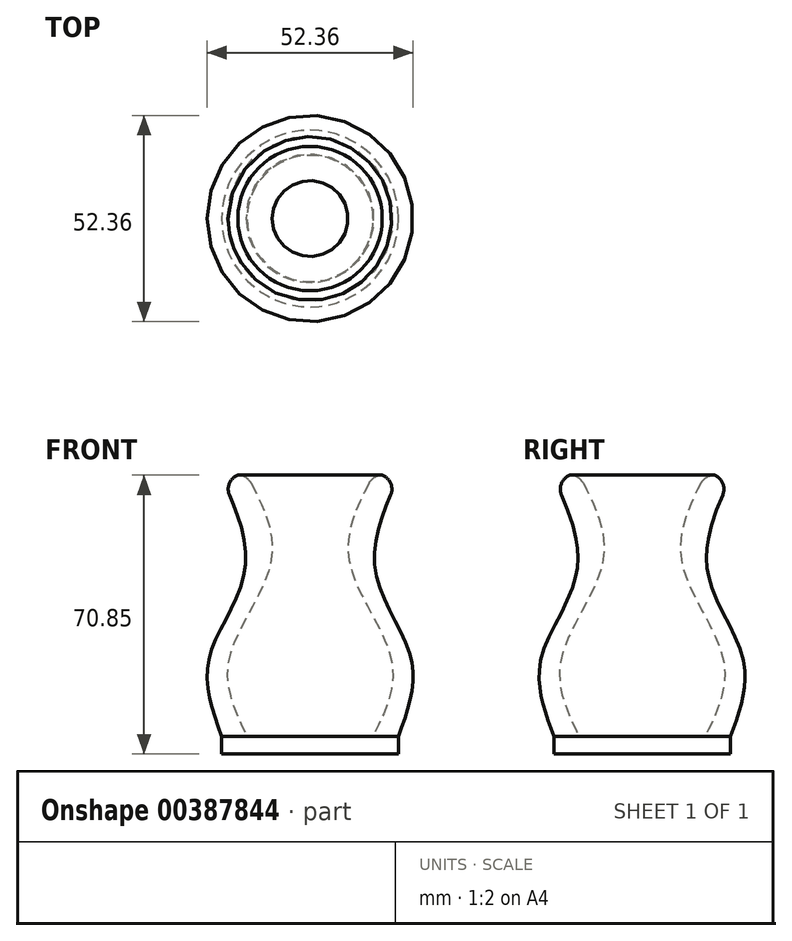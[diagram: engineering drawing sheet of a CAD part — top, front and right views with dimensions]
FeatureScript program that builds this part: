
annotation { "Feature Type Name" : "Feature", "Feature Type Description" : "" }
export const myFeature = defineFeature(function(context is Context, id is Id, definition is map)
    precondition{}
    {
        {
            var Q0;
            Q0=qCreatedBy(makeId("Front.planeOp"),FACE);
            var sketch = newSketch(context, id + "F0", { "sketchPlane" : qUnion([Q0])});
            skLineSegment(sketch, "E0", {"start": v(0, 0) * mm, "end": v(22.44, 0) * mm});
            skLineSegment(sketch, "E1", {"start": v(22.44, 0) * mm, "end": v(22.44, 4.52) * mm});
            skLineSegment(sketch, "E2", {"start": v(22.44, 4.52) * mm, "end": v(0, 4.52) * mm});
            skLineSegment(sketch, "E3", {"start": v(0, 4.52) * mm, "end": v(0, 0) * mm});
            skFitSpline(sketch, "E4", {"points": [v(22.44, 4.52) * mm, v(25.65, 24.34) * mm, v(16.32, 49.7) * mm, v(22.44, 70.4) * mm, v(22.44, 70.97) * mm], "startDerivative": vector(24.4, 66.3) * mm, "endDerivative": vector(-2.72, 7.27) * mm});
            skLineSegment(sketch, "E5", {"start": v(22.49, 70.85) * mm, "end": v(16.03, 70.85) * mm});
            skFitSpline(sketch, "E6", {"points": [v(16.03, 70.85) * mm, v(9.91, 49.11) * mm, v(20.7, 23.75) * mm, v(16.03, 4.52) * mm], "startDerivative": vector(-34.07, -64.64) * mm, "endDerivative": vector(-29.38, -60.4) * mm});
            skLineSegment(sketch, "E7", {"start": v(0, 0) * mm, "end": v(0, 76.46) * mm, "construction": true});
            skSolve(sketch);
        }
        {
            var Q0;
            {var subQ3=sQuery(id+"F0.wireOp",EDGE,"E6");Q0=makeQuery(id+"F0.imprint","IMPRINT",FACE,{"disambiguationData":[TD([[makeQuery(id+"F0.imprint","IMPRINT",EDGE,{"derivedFrom":subQ3}),1.0]])]});}
            var Q1;
            Q1=makeQuery(id+"F0.imprint","IMPRINT",FACE,{"disambiguationData":[TD([[makeQuery(id+"F0.imprint","IMPRINT",EDGE,{"derivedFrom":sQuery(id+"F0.wireOp",EDGE,"E0")}),1.0]])]});
            var Q2;
            Q2=sQuery(id+"F0.wireOp",EDGE,"E7");
            revolve(context, id + "F1", {"entities" : qUnion([Q0, Q1]), "axis" : qUnion([Q2]), "revolveType" : RevolveType.FULL});
        }
        {
            var Q0;
            Q0=makeQuery(id+"F1.opRevolve","SWEPT_EDGE",EDGE,{"disambiguationData":[OSD([sQuery(id+"F0.wireOp",EDGE,"E5"),sQuery(id+"F0.wireOp",EDGE,"E6")])]});
            fillet(context, id + "F2", {"entities" : qUnion([Q0]), "radius" : 3.8 * mm, "tangentPropagation" : true, "allowEdgeOverflow" : false});
        }
        {
            var Q0;
            Q0=makeQuery(id+"F1.opRevolve","SWEPT_EDGE",EDGE,{"disambiguationData":[OSD([sQuery(id+"F0.wireOp",EDGE,"E4"),sQuery(id+"F0.wireOp",EDGE,"E5")])]});
            fillet(context, id + "F3", {"entities" : qUnion([Q0]), "radius" : 3.8 * mm, "tangentPropagation" : true, "allowEdgeOverflow" : false});
        }
    });
